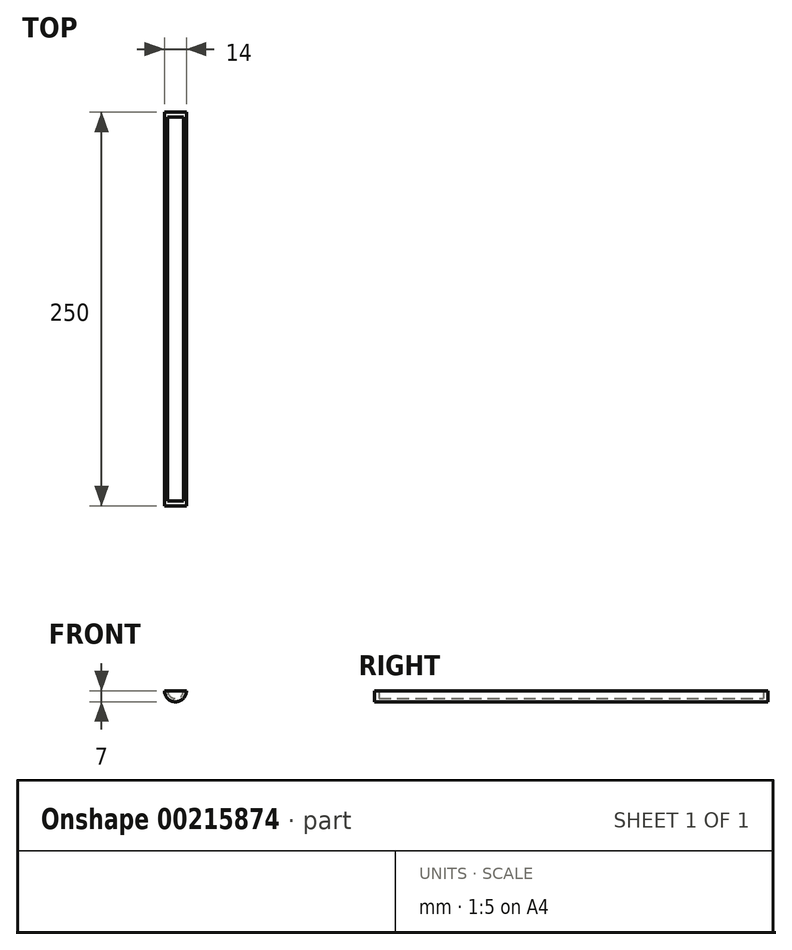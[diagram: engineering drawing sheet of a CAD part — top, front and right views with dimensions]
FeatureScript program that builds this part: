
annotation { "Feature Type Name" : "Feature", "Feature Type Description" : "" }
export const myFeature = defineFeature(function(context is Context, id is Id, definition is map)
    precondition{}
    {
        {
            var Q0;
            Q0=qCreatedBy(makeId("Front.planeOp"),FACE);
            var sketch = newSketch(context, id + "F0", { "sketchPlane" : qUnion([Q0])});
            skArc(sketch, "E0", {"start": v(-11.57, 7) * mm, "mid": v(-4.57, 0) * mm, "end": v(2.43, 7) * mm});
            skArc(sketch, "E1", {"start": v(-9.57, 7) * mm, "mid": v(-4.57, 2) * mm, "end": v(0.43, 7) * mm});
            skLineSegment(sketch, "E2", {"start": v(-11.57, 7) * mm, "end": v(-9.57, 7) * mm});
            skPoint(sketch, "E3.orphan", {"position": v(-28.27, 7) * mm});
            skLineSegment(sketch, "E4.trimOffspring", {"start": v(0.43, 7) * mm, "end": v(2.43, 7) * mm});
            skSolve(sketch);
        }
        {
            var Q0;
            Q0=makeQuery(id+"F0.imprint","IMPRINT",FACE,{"disambiguationData":[TD([[makeQuery(id+"F0.imprint","IMPRINT",EDGE,{"derivedFrom":sQuery(id+"F0.wireOp",EDGE,"E0")}),1.0]])]});
            extrude(context, id + "F1", {"entities" : qUnion([Q0]), "endBound" : BoundingType.SYMMETRIC, "depth" : 250 * mm});
        }
        {
            var Q0;
            Q0=makeQuery(id+"F1.opExtrude","CAP_FACE",FACE,{"disambiguationData":[OSD([sQuery(id+"F0.wireOp",EDGE,"E0"),sQuery(id+"F0.wireOp",EDGE,"E1"),sQuery(id+"F0.wireOp",EDGE,"E2"),sQuery(id+"F0.wireOp",EDGE,"E4.trimOffspring")])],"isStart":false});
            var sketch = newSketch(context, id + "F2", { "sketchPlane" : qUnion([Q0])});
            skLineSegment(sketch, "E5", {"start": v(-9.57, 7) * mm, "end": v(0.43, 7) * mm});
            skSolve(sketch);
        }
        {
            var Q0;
            Q0=makeQuery(id+"F2.imprint","IMPRINT",FACE,{"disambiguationData":[TD([[makeQuery(id+"F2.imprint","IMPRINT",EDGE,{"derivedFrom":sQuery(id+"F2.wireOp",EDGE,"E5")}),-1.0]])]});
            extrude(context, id + "F3", {"entities" : qUnion([Q0]), "operationType" : NewBodyOperationType.ADD, "oppositeDirection" : true, "depth" : 3 * mm});
        }
        {
            var Q0;
            Q0=makeQuery(id+"F1.opExtrude","CAP_FACE",FACE,{"disambiguationData":[OSD([sQuery(id+"F0.wireOp",EDGE,"E0"),sQuery(id+"F0.wireOp",EDGE,"E1"),sQuery(id+"F0.wireOp",EDGE,"E2"),sQuery(id+"F0.wireOp",EDGE,"E4.trimOffspring")])],"isStart":true});
            var sketch = newSketch(context, id + "F4", { "sketchPlane" : qUnion([Q0])});
            skLineSegment(sketch, "E6", {"start": v(-0.43, 7) * mm, "end": v(9.57, 7) * mm});
            skSolve(sketch);
        }
        {
            var Q0;
            Q0=makeQuery(id+"F4.imprint","IMPRINT",FACE,{"disambiguationData":[TD([[makeQuery(id+"F4.imprint","IMPRINT",EDGE,{"derivedFrom":sQuery(id+"F4.wireOp",EDGE,"E6")}),-1.0]])]});
            extrude(context, id + "F5", {"entities" : qUnion([Q0]), "operationType" : NewBodyOperationType.ADD, "oppositeDirection" : true, "depth" : 3 * mm});
        }
    });
